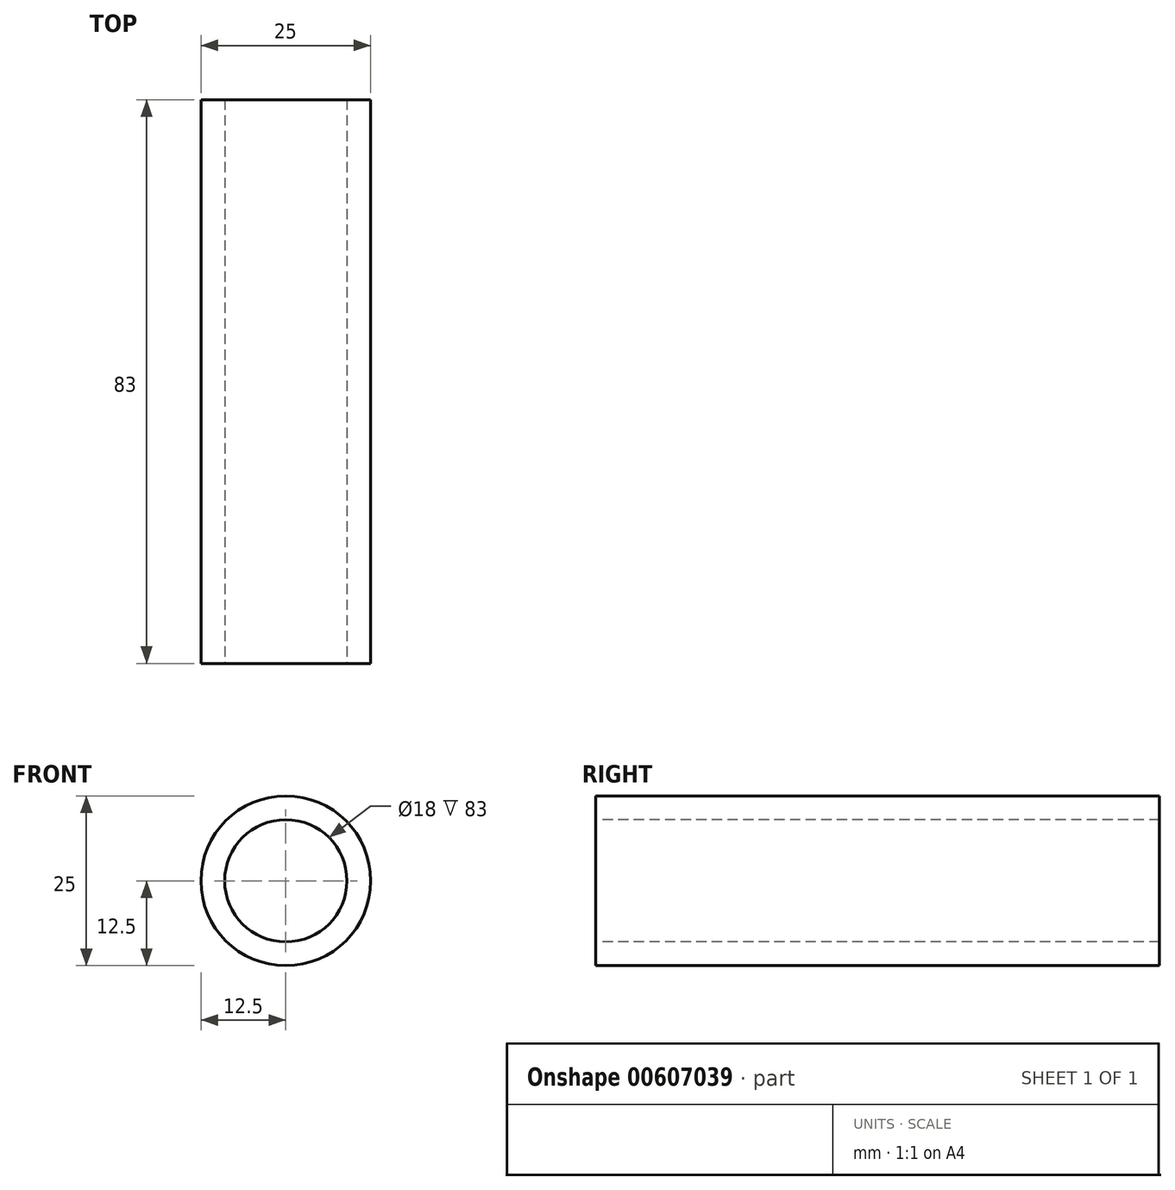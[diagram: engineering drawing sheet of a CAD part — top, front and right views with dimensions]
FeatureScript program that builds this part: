
annotation { "Feature Type Name" : "Feature", "Feature Type Description" : "" }
export const myFeature = defineFeature(function(context is Context, id is Id, definition is map)
    precondition{}
    {
        {
            var Q0;
            Q0=qCreatedBy(makeId("Front.planeOp"),FACE);
            var sketch = newSketch(context, id + "F0", { "sketchPlane" : qUnion([Q0]) });
            skCircle(sketch, "E0", {"center": v(0, 0) * mm, "radius": 12.5 * mm});
            skSolve(sketch);
        }
        {
            var Q0;
            Q0=makeQuery(id+"F0.imprint","IMPRINT",FACE,{"disambiguationData":[TD([[makeQuery(id+"F0.imprint","IMPRINT",EDGE,{"derivedFrom":sQuery(id+"F0.wireOp",EDGE,"E0")}),1.0]])]});
            extrude(context, id + "F1", {"entities" : qUnion([Q0]), "depth" : 83 * mm, "offsetDistance" : 25 * mm});
        }
        {
            var Q0;
            Q0=makeQuery(id+"F1.opExtrude","CAP_FACE",FACE,{"disambiguationData":[OSD([sQuery(id+"F0.wireOp",EDGE,"E0")])],"isStart":false});
            var sketch = newSketch(context, id + "F2", { "sketchPlane" : qUnion([Q0]) });
            skCircle(sketch, "E1", {"center": v(0, 0) * mm, "radius": 9 * mm});
            skSolve(sketch);
        }
        {
            var Q0;
            Q0=makeQuery(id+"F2.imprint","IMPRINT",FACE,{"disambiguationData":[TD([[makeQuery(id+"F2.imprint","IMPRINT",EDGE,{"derivedFrom":sQuery(id+"F2.wireOp",EDGE,"E1")}),1.0]])]});
            extrude(context, id + "F3", {"entities" : qUnion([Q0]), "operationType" : NewBodyOperationType.REMOVE, "endBound" : BoundingType.THROUGH_ALL, "oppositeDirection" : true, "depth" : 25 * mm, "offsetDistance" : 25 * mm});
        }
    });
